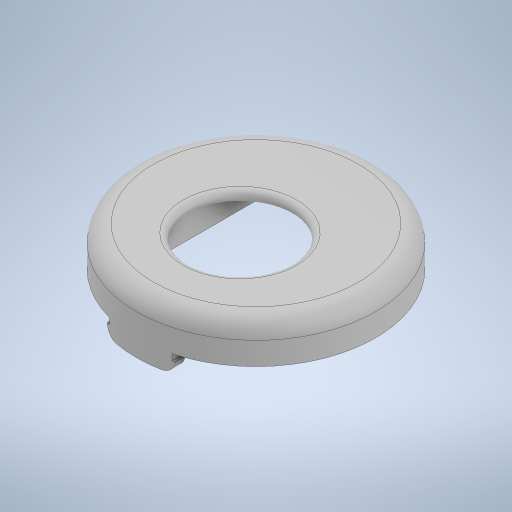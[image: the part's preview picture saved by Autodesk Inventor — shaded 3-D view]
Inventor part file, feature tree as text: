
AUTODESK INVENTOR PART (.ipt)
format: ipt  version: 2023 (Build 270158000, 158)  size: 412,672 bytes
history: mixed  units: in
note: dims shown in document units (in); Inventor stores cm internally (conversion verified against a paired STEP export)
features: sketch x9, extrude x9, move_body x2, projected_geometry x2, fillet x1, other x1, imported_body x1
ambient origin geometry x8: Origin, YZ Plane, XZ Plane, XY Plane, X Axis, Y Axis, Z Axis, Center Point
bodies: Solid1 (imported_parasolid)
feature tree (25):
  sketch  "Sketch2"  dims[d0=0.3937in d1=0.0in d2=0.3937in d3=0.0in]
  extrude  "Extrusion1"  Depth=0.3937in TaperAngle=0.0deg
  extrude  "Extrusion2"  Depth=0.3937in TaperAngle=0.0deg
  extrude  "Extrusion3"  Depth=0.3937in TaperAngle=0.0deg
  extrude  "Extrusion4"  TaperAngle=90.0deg  [1 undecoded]
  extrude  "Extrusion5"  Depth=0.3937in TaperAngle=0.0deg
  extrude  "Extrusion6"  Depth=0.0472in
  sketch  "Sketch8"  dims[d18=0.0185in d20=0.0472in]
  extrude  "Extrusion7"  Depth=0.0394in
  extrude  "Extrusion8"  [1 undecoded]
  extrude  "Extrusion9"  [1 undecoded]
  fillet  "Fillet1"  [1 undecoded]
  move_body  "Move Body1"
  move_body  "Move Body2"
  sketch  "Sketch3"  dims[d4=0.3937in d5=0.0in d6=0.3937in d7=0.0in]
  sketch  "Sketch4"  dims[d8=0.3937in d9=0.0in d10=0.0787in d11=0.0in]
  projected_geometry  "Projected Loop1"
  sketch  "Sketch6"  dims[d12=0.1181in d13=90.0deg]
  projected_geometry  "Projected Loop2"
  sketch  "Sketch7"  dims[d14=0.3937in d15=0.0in d16=0.3937in d17=0.0in]
  sketch  "Sketch9"  dims[d21=0.0in d22=0.0in d23=0.0394in]
  sketch  "Sketch10"  dims[d24=90.0deg d25=-0.6184in]
  sketch  "Sketch12"
  other  "Top"
  imported_body  NMx_Import_Brep_tag  [imported B-rep: ~5 faces, bbox_mm=None]
note: 4 required parameter values undecoded (feature->parameter linkage not recoverable at this tier; creation-order binding heuristic only, values carry confidence <= 0.55)
